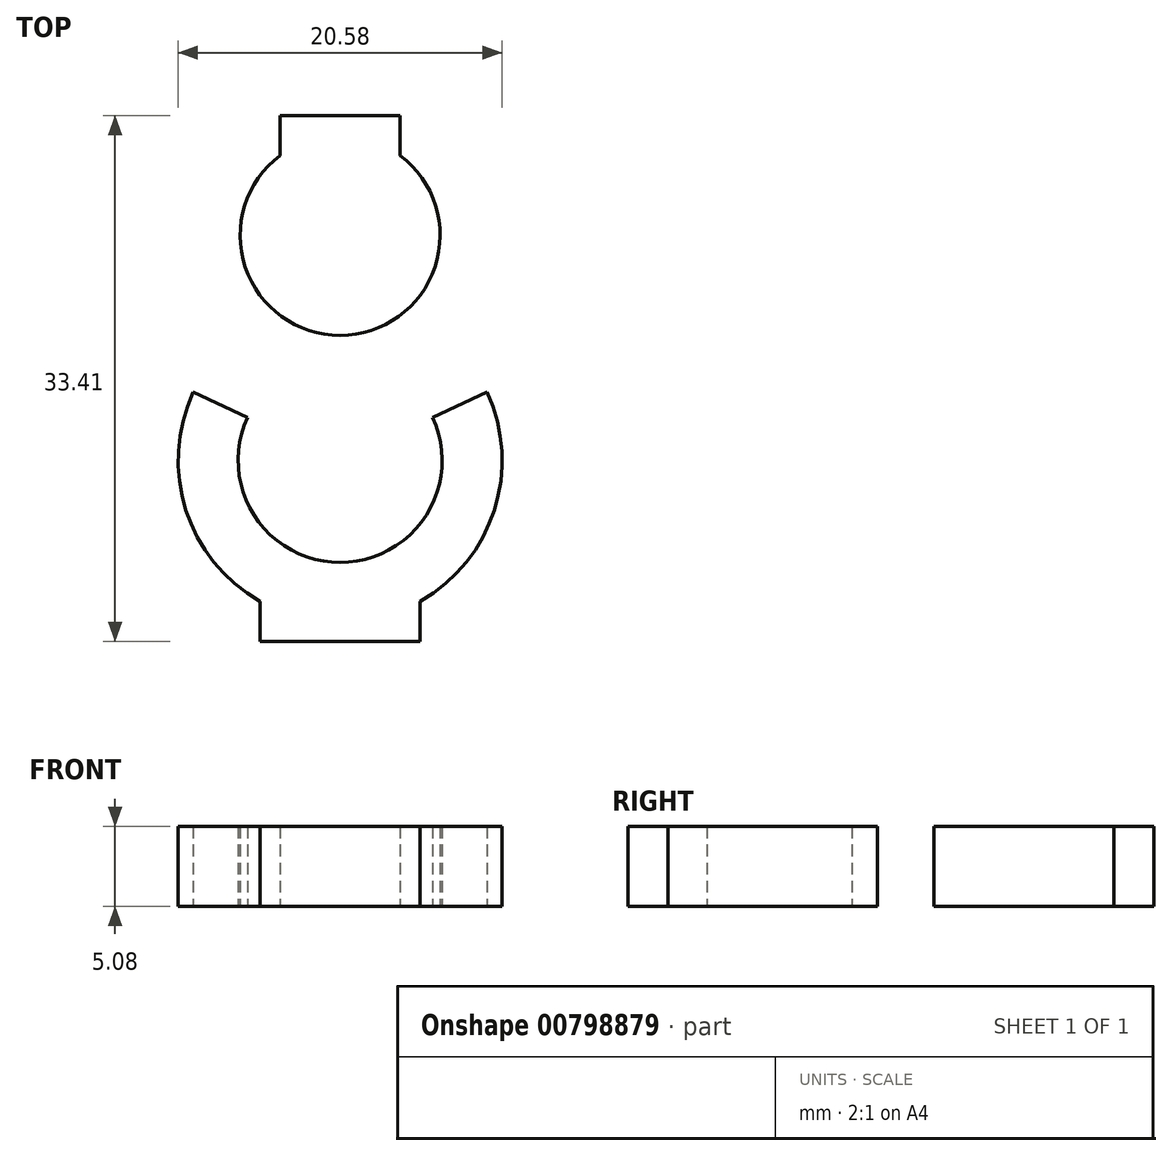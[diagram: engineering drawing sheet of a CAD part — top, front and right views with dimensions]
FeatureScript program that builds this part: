
annotation { "Feature Type Name" : "Feature", "Feature Type Description" : "" }
export const myFeature = defineFeature(function(context is Context, id is Id, definition is map)
    precondition{}
    {
        {
            var Q0;
            Q0=qCreatedBy(makeId("Top.planeOp"),FACE);
            var sketch = newSketch(context, id + "F0", { "sketchPlane" : qUnion([Q0])});
            skLineSegment(sketch, "E0.bottom", {"start": v(-3.81, 0) * mm, "end": v(3.81, 0) * mm, "construction": true});
            skLineSegment(sketch, "E0.top", {"start": v(-3.81, 7.62) * mm, "end": v(0, 7.62) * mm});
            skLineSegment(sketch, "E0.left", {"start": v(-3.81, 0) * mm, "end": v(-3.81, 5.08) * mm, "construction": true});
            skLineSegment(sketch, "E0.right", {"start": v(3.81, 0) * mm, "end": v(3.81, 5.08) * mm, "construction": true});
            skPoint(sketch, "E1", {"position": v(0, 7.62) * mm});
            skPoint(sketch, "E1.positionSnap0", {"position": v(0, 7.62) * mm});
            skLineSegment(sketch, "E2", {"start": v(0, 7.62) * mm, "end": v(3.81, 7.62) * mm});
            skPoint(sketch, "E3", {"position": v(3.81, 5.08) * mm});
            skPoint(sketch, "E4", {"position": v(-3.81, 5.08) * mm});
            skLineSegment(sketch, "E5", {"start": v(3.81, 5.08) * mm, "end": v(3.81, 7.62) * mm});
            skLineSegment(sketch, "E6", {"start": v(-3.81, 5.08) * mm, "end": v(-3.81, 7.62) * mm});
            skArc(sketch, "E7", {"start": v(-3.81, 5.08) * mm, "mid": v(0, -6.35) * mm, "end": v(3.81, 5.08) * mm});
            skArc(sketch, "E8", {"start": v(3.81, 5.08) * mm, "mid": v(0, 6.35) * mm, "end": v(-3.81, 5.08) * mm, "construction": true});
            skSolve(sketch);
        }
        {
            var Q0;
            Q0=qCreatedBy(makeId("Top.planeOp"),FACE);
            var sketch = newSketch(context, id + "F1", { "sketchPlane" : qUnion([Q0])});
            skLineSegment(sketch, "E9", {"start": v(0, 0) * mm, "end": v(-5.87, 2.74) * mm, "construction": true});
            skPoint(sketch, "E10", {"position": v(-5.87, 2.74) * mm});
            skLineSegment(sketch, "E11", {"start": v(0, -10.29) * mm, "end": v(0, 0) * mm, "construction": true});
            skLineSegment(sketch, "E12.MirrorCS", {"start": v(0, 0) * mm, "end": v(5.87, 2.74) * mm, "construction": true});
            skPoint(sketch, "E13.MirrorP", {"position": v(5.87, 2.74) * mm});
            skLineSegment(sketch, "E14", {"start": v(0, 0) * mm, "end": v(-10.29, 0) * mm, "construction": true});
            skLineSegment(sketch, "E15", {"start": v(-9.32, 4.35) * mm, "end": v(-9.32, 4.35) * mm});
            skArc(sketch, "E16", {"start": v(-9.32, 4.35) * mm, "mid": v(-9.8, -3.13) * mm, "end": v(-5.08, -8.95) * mm});
            skArc(sketch, "E17", {"start": v(-5.87, 2.74) * mm, "mid": v(-5.46, -3.48) * mm, "end": v(0, -6.48) * mm});
            skLineSegment(sketch, "E18", {"start": v(-5.87, 2.74) * mm, "end": v(-9.32, 4.35) * mm});
            skLineSegment(sketch, "E19", {"start": v(5.87, 2.74) * mm, "end": v(5.87, 2.74) * mm});
            skLineSegment(sketch, "E20", {"start": v(5.87, 2.74) * mm, "end": v(9.32, 4.35) * mm});
            skLineSegment(sketch, "E21", {"start": v(-5.08, -8.95) * mm, "end": v(-5.08, -11.49) * mm});
            skArc(sketch, "E22", {"start": v(0, -6.48) * mm, "mid": v(5.46, -3.48) * mm, "end": v(5.87, 2.74) * mm});
            skArc(sketch, "E23", {"start": v(-5.08, -8.95) * mm, "mid": v(-2.63, -9.95) * mm, "end": v(0, -10.29) * mm, "construction": true});
            skLineSegment(sketch, "E24", {"start": v(0, -10.29) * mm, "end": v(0, -10.29) * mm});
            skLineSegment(sketch, "E25", {"start": v(5.08, -8.95) * mm, "end": v(5.08, -11.49) * mm});
            skLineSegment(sketch, "E26", {"start": v(5.08, -11.49) * mm, "end": v(-5.08, -11.49) * mm});
            skPoint(sketch, "E27.orphan", {"position": v(0, -11.49) * mm});
            skArc(sketch, "E28", {"start": v(5.08, -8.95) * mm, "mid": v(9.8, -3.13) * mm, "end": v(9.32, 4.35) * mm});
            skArc(sketch, "E29", {"start": v(0, -10.29) * mm, "mid": v(2.63, -9.95) * mm, "end": v(5.08, -8.95) * mm, "construction": true});
            skSolve(sketch);
        }
        {
            var Q0;
            Q0=makeQuery(id+"F1.imprint","IMPRINT",FACE,{"disambiguationData":[TD([[makeQuery(id+"F1.imprint","IMPRINT",EDGE,{"derivedFrom":sQuery(id+"F1.wireOp",EDGE,"E16")}),1.0]])]});
            var Q1;
            Q1 = qSketchRegion(id + "F0", true);
            extrude(context, id + "F2", {"entities" : qUnion([Q0, Q1]), "depth" : 5.08 * mm, "offsetDistance" : 25.4 * mm});
        }
        {
            var Q0;
            Q0=makeQuery(id+"F2.opExtrude","SWEPT_BODY",BODY,{"disambiguationData":[OSD([sQuery(id+"F1.wireOp",EDGE,"E16"),sQuery(id+"F1.wireOp",EDGE,"E17"),sQuery(id+"F1.wireOp",EDGE,"E18"),sQuery(id+"F1.wireOp",EDGE,"E20"),sQuery(id+"F1.wireOp",EDGE,"E21"),sQuery(id+"F1.wireOp",EDGE,"E22"),sQuery(id+"F1.wireOp",EDGE,"E25"),sQuery(id+"F1.wireOp",EDGE,"E26"),sQuery(id+"F1.wireOp",EDGE,"E28")])]});
            transform(context, id + "F3", {"entities" : qUnion([Q0]), "transformType" : TransformType.TRANSLATION_3D, "dx" : 0 * mm, "dy" : -14.3 * mm, "dz" : 0 * mm, "makeCopy" : false});
        }
    });
